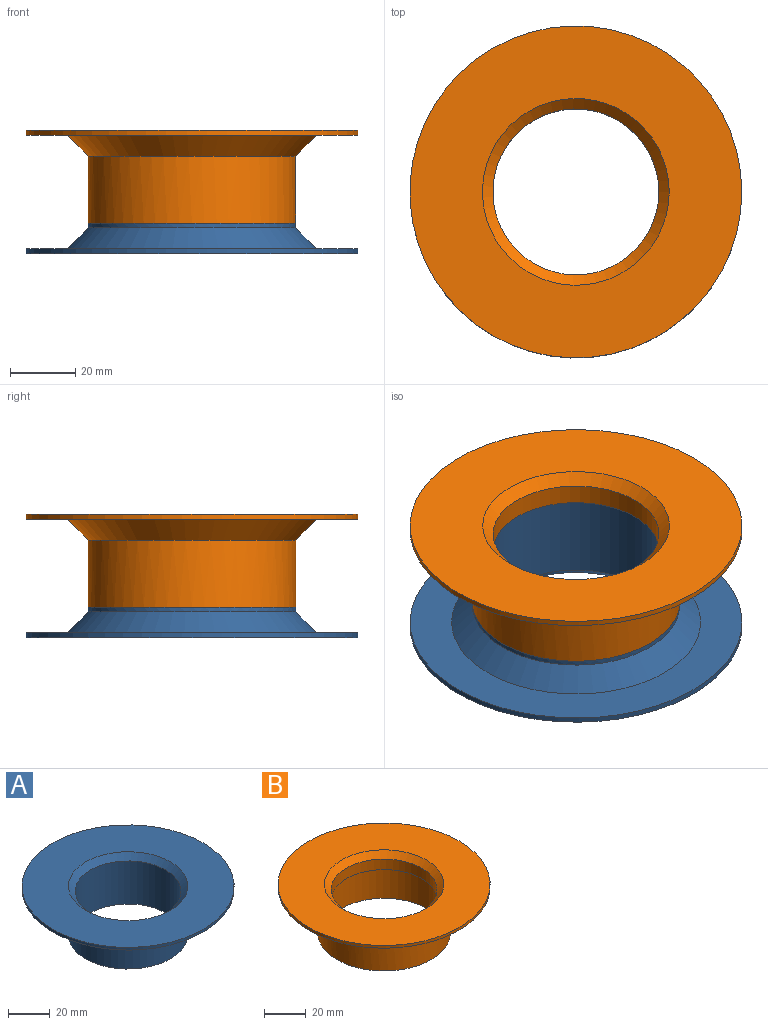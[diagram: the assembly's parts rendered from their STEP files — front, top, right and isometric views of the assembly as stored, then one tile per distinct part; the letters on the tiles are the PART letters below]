
ASSEMBLY  parts=2 mates=1
PART A: 10 faces, bbox 101.6x101.6x28.4 mm
  f0: cylinder r=31.75mm len=63.5mm, axis (0,0,1), area 285mm2, adj f7,f9
  f1: plane 57.15x57.15mm, normal (0,0,-1), area 538.4mm2, adj f2,f6
  f2: cylinder r=25.4mm len=50.8mm, axis (0,0,-1), area 4028.3mm2, adj f1,f8
  f3: cylinder r=50.8mm len=101.6mm, axis (0,0,-1), area 506.7mm2, adj f4,f5
  f4: plane 101.6x101.6mm, normal (0,0,1), area 5542.1mm2, adj f3,f8
  f5: plane 101.6x101.6mm, normal (0,0,-1), area 3547mm2, adj f3,f9
  f6: cylinder r=28.57mm len=57.15mm, axis (0,0,-1), area 3420.3mm2, adj f1,f7
  f7: plane 63.5x63.5mm, normal (0,0,-1), area 601.7mm2, adj f0,f6
  f8: cone r=25.4mm half-angle=45deg, axis (0,0,1), area 761.4mm2, adj f2,f4
  f9: cone r=31.75mm half-angle=45deg, axis (0,0,1), area 1970.6mm2, adj f0,f5
PART B: 10 faces, bbox 101.6x101.6x28.4 mm
  f0: cylinder r=25.4mm len=50.8mm, axis (0,0,-1), area 988.1mm2, adj f7,f8
  f1: cylinder r=50.8mm len=101.6mm, axis (0,0,-1), area 506.7mm2, adj f2,f3
  f2: plane 101.6x101.6mm, normal (0,0,1), area 5542.1mm2, adj f1,f8
  f3: plane 101.6x101.6mm, normal (0,0,-1), area 3547mm2, adj f1,f9
  f4: cylinder r=31.75mm len=63.5mm, axis (0,0,1), area 4085.3mm2, adj f5,f9
  f5: plane 63.5x63.5mm, normal (0,0,-1), area 601.7mm2, adj f4,f6
  f6: cylinder r=28.57mm len=57.15mm, axis (0,0,-1), area 3420.3mm2, adj f5,f7
  f7: plane 57.15x57.15mm, normal (0,0,-1), area 538.4mm2, adj f0,f6
  f8: cone r=25.4mm half-angle=45deg, axis (0,0,1), area 761.4mm2, adj f0,f2
  f9: cone r=31.75mm half-angle=45deg, axis (0,0,1), area 1970.6mm2, adj f3,f4
PLACE A rot(axis=(1,0,0),180deg) t=(-18.36,-8.69,-25.07)mm
PLACE B t=(-18.36,-8.69,9.54)mm
MATE fastened A.f0 <-> B.f4  axis (0,0,1) through (-18.36,-8.69,1.76)mm
